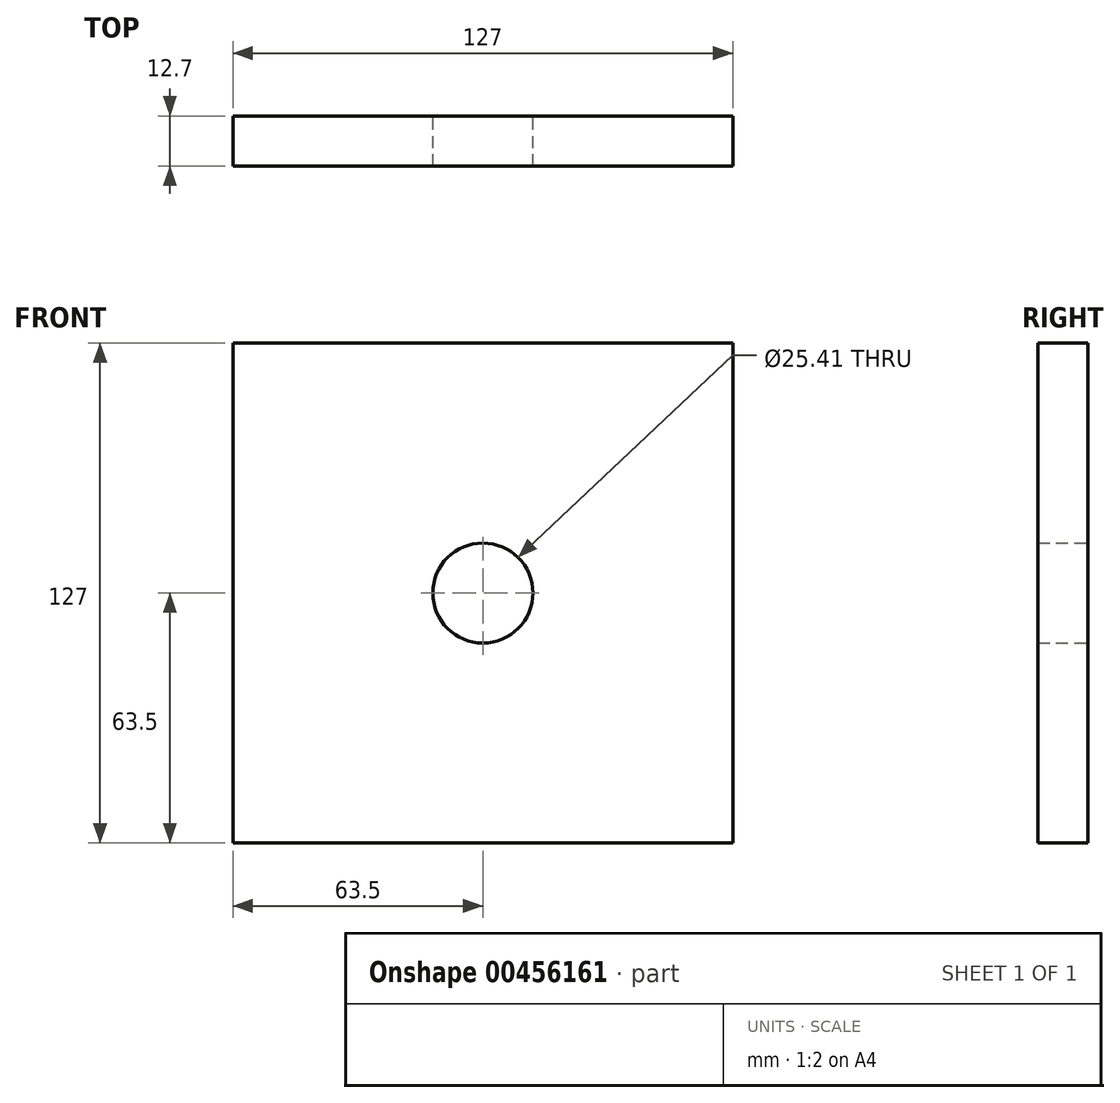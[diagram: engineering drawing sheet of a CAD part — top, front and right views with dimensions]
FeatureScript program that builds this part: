
annotation { "Feature Type Name" : "Feature", "Feature Type Description" : "" }
export const myFeature = defineFeature(function(context is Context, id is Id, definition is map)
    precondition{}
    {
        {
            var Q0;
            Q0=qCreatedBy(makeId("Front.planeOp"),FACE);
            var sketch = newSketch(context, id + "F0", { "sketchPlane" : qUnion([Q0])});
            skLineSegment(sketch, "E0.bottom", {"start": v(63.5, -63.5) * mm, "end": v(-63.5, -63.5) * mm});
            skLineSegment(sketch, "E0.top", {"start": v(63.5, 63.5) * mm, "end": v(-63.5, 63.5) * mm});
            skLineSegment(sketch, "E0.left", {"start": v(63.5, -63.5) * mm, "end": v(63.5, 63.5) * mm});
            skLineSegment(sketch, "E0.right", {"start": v(-63.5, -63.5) * mm, "end": v(-63.5, 63.5) * mm});
            skPoint(sketch, "E0.middle", {"position": v(0, 0) * mm});
            skCircle(sketch, "E1", {"center": v(0, 0) * mm, "radius": 12.7 * mm});
            skSolve(sketch);
        }
        {
            var Q0;
            Q0=makeQuery(id+"F0.imprint","IMPRINT",FACE,{"disambiguationData":[TD([[makeQuery(id+"F0.imprint","IMPRINT",EDGE,{"derivedFrom":sQuery(id+"F0.wireOp",EDGE,"E0.bottom")}),-1.0]])]});
            extrude(context, id + "F1", {"entities" : qUnion([Q0]), "depth" : 12.7 * mm});
        }
    });
